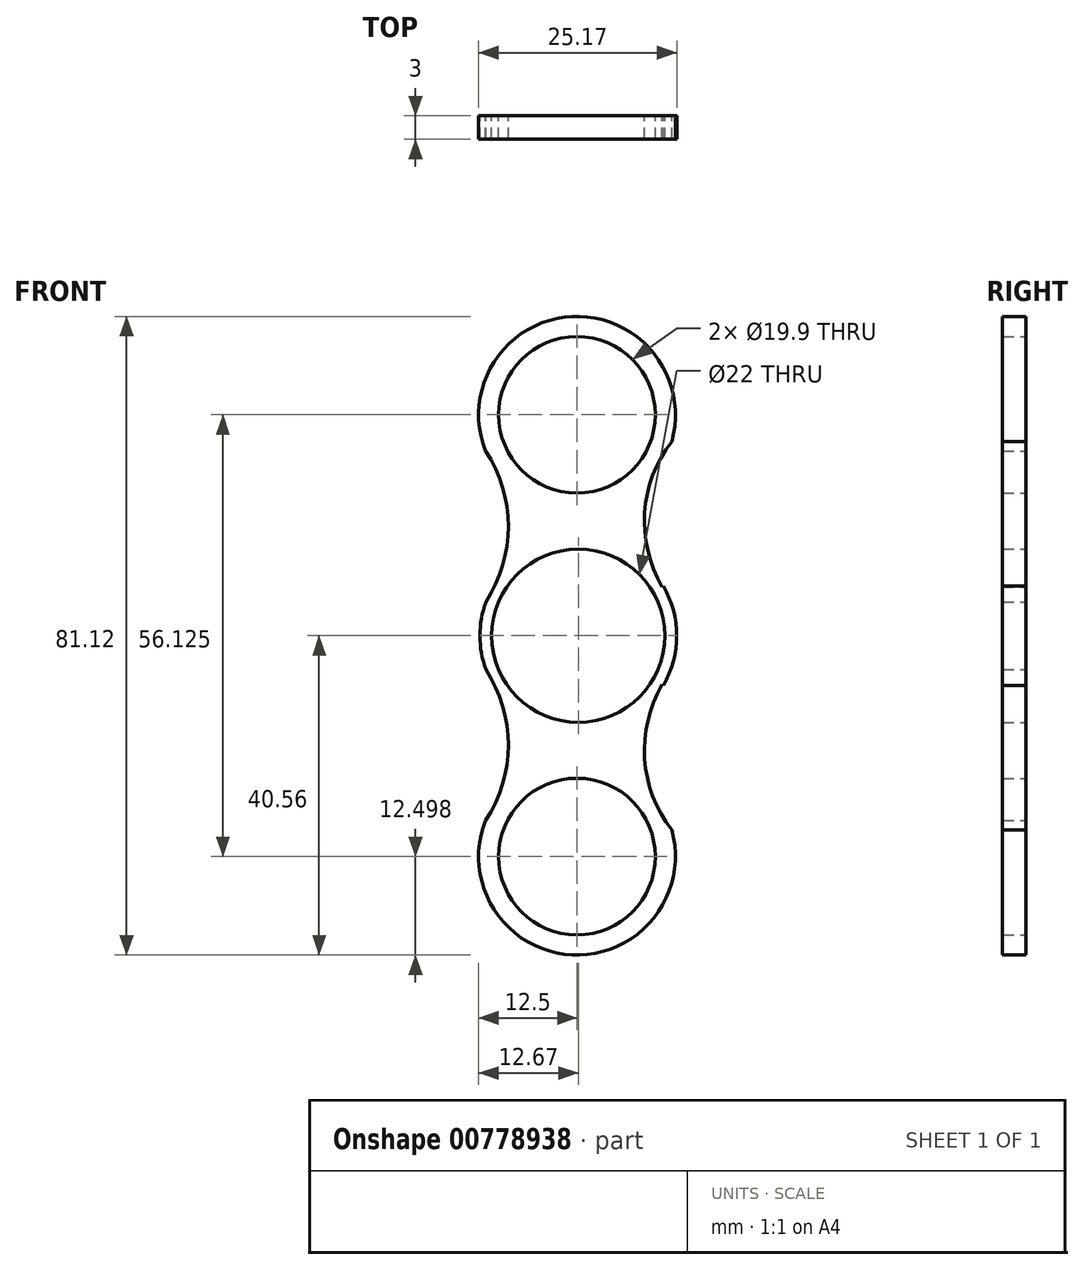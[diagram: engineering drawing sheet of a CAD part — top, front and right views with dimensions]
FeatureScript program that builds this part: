
annotation { "Feature Type Name" : "Feature", "Feature Type Description" : "" }
export const myFeature = defineFeature(function(context is Context, id is Id, definition is map)
    precondition{}
    {
        {
            var Q0;
            Q0=qCreatedBy(makeId("Front.planeOp"),FACE);
            var sketch = newSketch(context, id + "F0", { "sketchPlane" : qUnion([Q0])});
            skArc(sketch, "E0", {"start": v(11, 0) * mm, "mid": v(0, 11) * mm, "end": v(-11, 0) * mm});
            skCircle(sketch, "E1", {"center": v(-0.17, 28.06) * mm, "radius": 9.95 * mm});
            skArc(sketch, "E2", {"start": v(11.87, 24.68) * mm, "mid": v(-0.81, 40.55) * mm, "end": v(-11.8, 23.47) * mm});
            skArc(sketch, "E3", {"start": v(12.5, 0) * mm, "mid": v(12.07, 3.26) * mm, "end": v(10.8, 6.3) * mm});
            skLineSegment(sketch, "E4", {"start": v(10.65, 6.22) * mm, "end": v(10.8, 6.3) * mm});
            skArc(sketch, "E5", {"start": v(11.87, 24.68) * mm, "mid": v(8.43, 15.64) * mm, "end": v(10.65, 6.22) * mm});
            skArc(sketch, "E6.MirrorC", {"start": v(-11.8, 23.47) * mm, "mid": v(-0.81, 40.55) * mm, "end": v(11.87, 24.68) * mm});
            skArc(sketch, "E7.MirrorCS", {"start": v(-11.8, 23.47) * mm, "mid": v(-8.9, 13.9) * mm, "end": v(-11.73, 4.3) * mm});
            skPoint(sketch, "E8.orphan", {"position": v(-16.98, 0) * mm});
            skArc(sketch, "E9.trimOffspring", {"start": v(-11.73, 4.3) * mm, "mid": v(-12.3, 2.19) * mm, "end": v(-12.5, 0) * mm});
            skPoint(sketch, "E10.orphan", {"position": v(11.82, 4.47) * mm});
            skArc(sketch, "E11.MirrorCS", {"start": v(11, 0) * mm, "mid": v(0, -11) * mm, "end": v(-11, 0) * mm});
            skPoint(sketch, "E12.MirrorP", {"position": v(11.82, -4.47) * mm});
            skArc(sketch, "E13.MirrorCS", {"start": v(12.5, 0) * mm, "mid": v(12.07, -3.26) * mm, "end": v(10.8, -6.3) * mm});
            skLineSegment(sketch, "E14.MirrorCS", {"start": v(10.65, -6.22) * mm, "end": v(10.8, -6.3) * mm});
            skArc(sketch, "E15.MirrorCS", {"start": v(-11.73, -4.3) * mm, "mid": v(-12.3, -2.19) * mm, "end": v(-12.5, 0) * mm});
            skCircle(sketch, "E16.MirrorC", {"center": v(-0.17, -28.06) * mm, "radius": 9.95 * mm});
            skArc(sketch, "E17.MirrorC", {"start": v(-11.8, -23.47) * mm, "mid": v(-0.81, -40.55) * mm, "end": v(11.87, -24.68) * mm});
            skArc(sketch, "E18.MirrorCS", {"start": v(-11.8, -23.47) * mm, "mid": v(-8.9, -13.9) * mm, "end": v(-11.73, -4.3) * mm});
            skArc(sketch, "E19.MirrorCS", {"start": v(11.87, -24.68) * mm, "mid": v(8.43, -15.64) * mm, "end": v(10.65, -6.22) * mm});
            skArc(sketch, "E20.trimOffspring", {"start": v(11.87, -24.68) * mm, "mid": v(-0.81, -40.55) * mm, "end": v(-11.8, -23.47) * mm});
            skPoint(sketch, "E21.orphan", {"position": v(26.7, 0) * mm});
            skSolve(sketch);
        }
        {
            var Q0;
            Q0 = qSketchRegion(id + "F0", true);
            extrude(context, id + "F1", {"entities" : qUnion([Q0]), "depth" : (3) * mm, "offsetDistance" : 25 * mm});
        }
    });
